# Revit family: Drinking_Fountain-Haws_Corporation-Wall_Mounted_1311
name_source: partatom
category: Plumbing Fixtures
units: mm (PartAtom-declared; Revit-internal decimal feet)

## family parameters
Always vertical = Yes
Cut with Voids When Loaded = No
Host = Wall
OmniClass Number = 23.65.70.14.11
OmniClass Title = Drinking Fountains/Coolers
Part Type = Normal
Room Calculation Point = No
Round Connector Dimension = Use Radius
Shared = Yes

## types (5) — shared parameters
Assembly Code = D2010810
BIMobject category = Taps & Mixers
BIMobject category code = sanitary-taps-mixers
BIMobject main category = Sanitary
BIMobject main category code = sanitary
Basin Height = 6"
Bowl = Metal - Haws Corporation - White Enameled Iron
Brand url = https://www.hawsco.com
CW Connection = Yes
CWFU = 1
Cost = $0
Cost Note = For Cost information please visit the Resource tab in the Product Page URL
Date of publishing = 3/24/2014
Design country = United States
EAN code = https://611970318981
Edition number = 1
Flow = 0.00 GPM
Fountain Level = 27"
HW Connection = No
Keynote = 15410.A1
Manufacturer = Haws Corporation 1455 Kleppe Lane Sparks, NV 89431
Manufacturer country = United States
Manufacturer name = Haws Corporation
Masterformat 2014 Code = 22 47 13
Masterformat 2014 Description = Drinking Fountains
Material main = Metal
Nominal height = 8"
Nominal width = 14"
OmniClass Code = 23-31 31 00
OmniClass Description = Drinking Fountains
Product Guid = e3c02aa8-b1e5-48e9-8e2c-075754d90ad4
Product Page URL = https://www.hawsco.com
Product SKU = haws-1311
Product certification = http://www.csagroup.org
Product data url = https://www.bimobject.com
Product family = Drinking Fountains/Coolers
Product group = Wall Mounted Drinking Fountains
Sanitary Radius = 5/8"
Series = The Haws 1311enameled iron, barrier-free drinking fountain
Supply Radius = 3/16"
Trap = Metal - Haws Corporation - Copper Poly
Tubing = Metal - Haws Corporation - Copper Poly
Type Comments = Gleaming white enameled iron construction
URL = http://www.hawsco.com
Uniclass 1.4 Code = L7213
Uniclass 1.4 Description = Fountains
Uniclass 2.0 Code = SS-35-65-70-25
Uniclass 2.0 Description = Drinking Fountain Systems
Uniclass 2015 Code = Pr_40_20_87_24
Uniclass 2015 Name = Drinking fountains
Vent Connection = No
WFU = 1
Waste Connection = Yes
Waste Level = 29 3/8"
Weight Net (Kg) = 50
zero-valued in all types: HWFU

## per-type parameters (varying)
| type | BP15W Panel | BP8W Panel | Bottle Filler 1920W | Description | Supply_No | z_8wor15w | z_notPanel |
| 1311 | No | No | No | Bullet proof durability hidden beneath its elegant appeal | 2 | No | Yes |
| 1311-1920W | No | No | Yes | Beautiful white enamel fountain and powder-coated bottle filler combination brings pleasing aesthetics to any environment | 3 | No | Yes |
| 1311-BP8W-1920W | No | Yes | Yes | Beautiful white enamel fountain and powder-coated bottle filler combination brings pleasing aesthetics to any environment | 3 | Yes | No |
| 1311-1920W-BP15W | Yes | No | Yes | Beautiful white enamel fountain and powder-coated bottle filler combination brings pleasing aesthetics to any environment | 3 | Yes | No |
| 1311-BP8W-1920W-BP15W | Yes | Yes | Yes | Beautiful white enamel fountain and powder-coated bottle filler combination brings pleasing aesthetics to any environment | 3 | Yes | No |

note: column(s) folded — value = type name in every type: Model

## geometry (parser evidence)
native form markers: Blend x14, Sweep x8
no freeform markers — native parametric forms only
